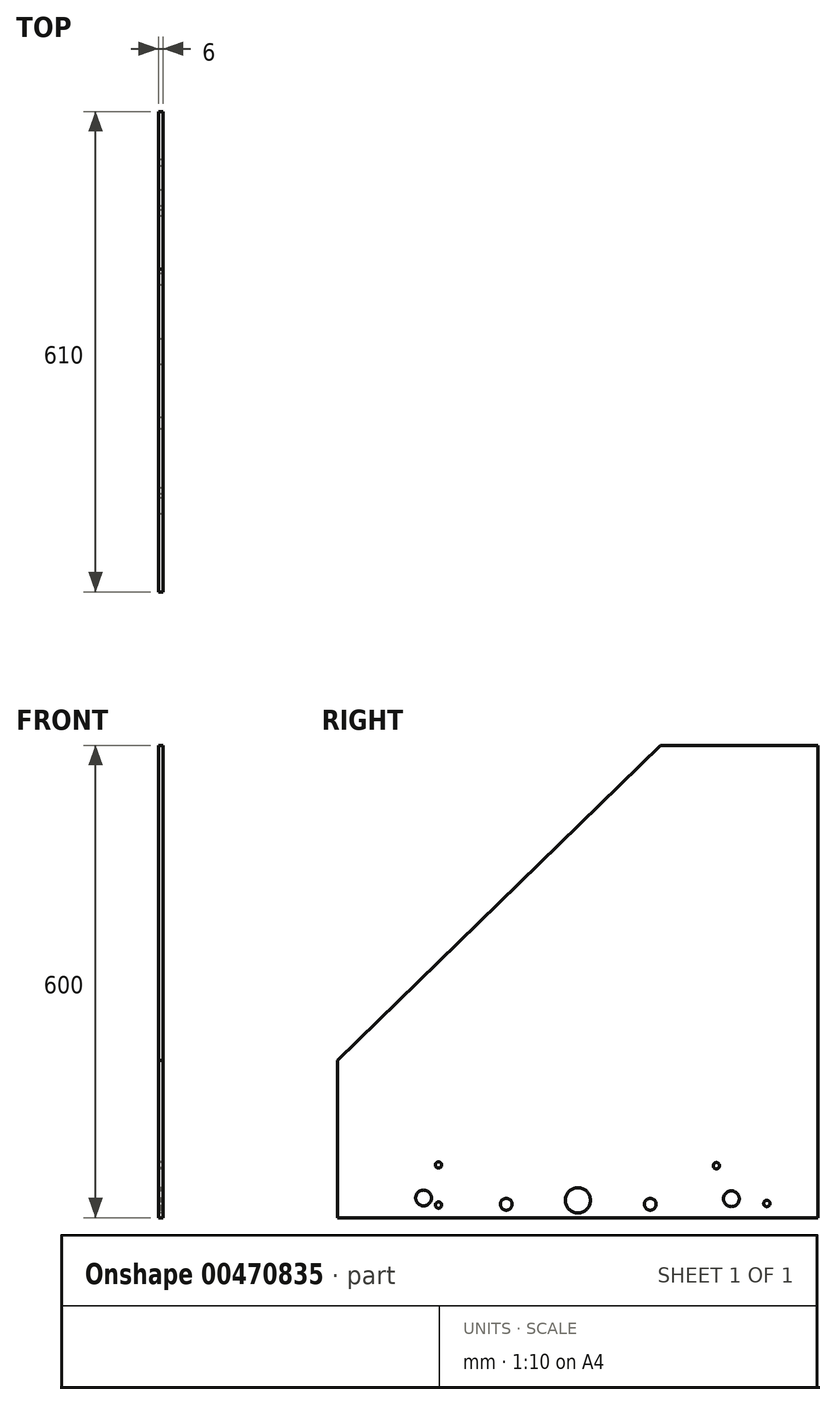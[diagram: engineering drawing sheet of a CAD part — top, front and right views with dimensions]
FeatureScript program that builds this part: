
annotation { "Feature Type Name" : "Feature", "Feature Type Description" : "" }
export const myFeature = defineFeature(function(context is Context, id is Id, definition is map)
    precondition{}
    {
        {
            var Q0;
            Q0=qCreatedBy(makeId("Right.planeOp"),FACE);
            var sketch = newSketch(context, id + "F0", { "sketchPlane" : qUnion([Q0])});
            skLineSegment(sketch, "E0", {"start": v(0, 0) * mm, "end": v(-610, 0) * mm});
            skLineSegment(sketch, "E1", {"start": v(-610, 0) * mm, "end": v(-610, 200) * mm});
            skLineSegment(sketch, "E2", {"start": v(0, 0) * mm, "end": v(0, 600) * mm});
            skLineSegment(sketch, "E3", {"start": v(0, 600) * mm, "end": v(-200, 600) * mm});
            skLineSegment(sketch, "E4", {"start": v(-610, 200) * mm, "end": v(-200, 600) * mm});
            skCircle(sketch, "E5", {"center": v(-65, 18) * mm, "radius": 4 * mm});
            skCircle(sketch, "E6", {"center": v(-110, 24) * mm, "radius": 10 * mm});
            skCircle(sketch, "E7", {"center": v(-129, 66) * mm, "radius": 4 * mm});
            skCircle(sketch, "E8", {"center": v(-213, 17) * mm, "radius": 7.5 * mm});
            skCircle(sketch, "E9", {"center": v(-305, 22) * mm, "radius": 16 * mm});
            skCircle(sketch, "E10", {"center": v(-396, 17) * mm, "radius": 7.5 * mm});
            skCircle(sketch, "E11", {"center": v(-482, 67) * mm, "radius": 4 * mm});
            skCircle(sketch, "E12", {"center": v(-482, 16) * mm, "radius": 4 * mm});
            skLineSegment(sketch, "E13", {"start": v(0, 0) * mm, "end": v(-496, 0) * mm});
            skCircle(sketch, "E14", {"center": v(-501, 25) * mm, "radius": 10 * mm});
            skSolve(sketch);
        }
        {
            var Q0;
            Q0=makeQuery(id+"F0.imprint","IMPRINT",FACE,{"disambiguationData":[TD([[makeQuery(id+"F0.imprint","IMPRINT",EDGE,{"derivedFrom":sQuery(id+"F0.wireOp",EDGE,"E0")}),-1.0]])]});
            extrude(context, id + "F1", {"entities" : qUnion([Q0]), "depth" : 6 * mm});
        }
    });
